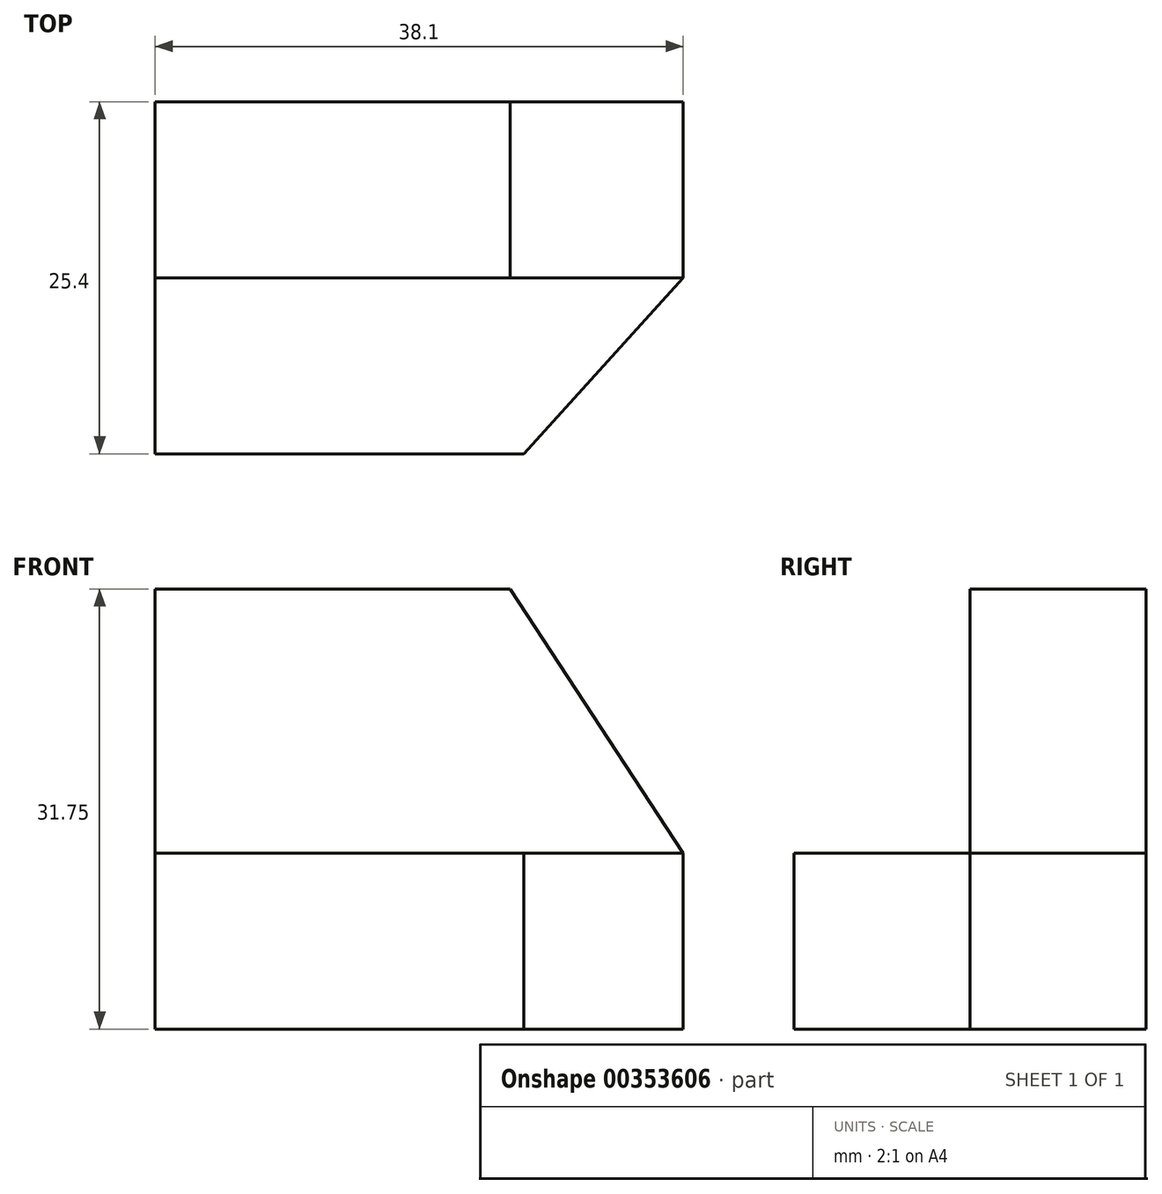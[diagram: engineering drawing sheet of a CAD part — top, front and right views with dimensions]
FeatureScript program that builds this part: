
annotation { "Feature Type Name" : "Feature", "Feature Type Description" : "" }
export const myFeature = defineFeature(function(context is Context, id is Id, definition is map)
    precondition{}
    {
        {
            var Q0;
            Q0=qCreatedBy(makeId("Right.planeOp"),FACE);
            var sketch = newSketch(context, id + "F0", { "sketchPlane" : qUnion([Q0])});
            skLineSegment(sketch, "E0", {"start": v(0, 0) * mm, "end": v(0, 31.75) * mm});
            skLineSegment(sketch, "E1", {"start": v(0, 31.75) * mm, "end": v(-12.7, 31.75) * mm});
            skLineSegment(sketch, "E2", {"start": v(-12.7, 31.75) * mm, "end": v(-12.7, 12.7) * mm});
            skLineSegment(sketch, "E3", {"start": v(-12.7, 12.7) * mm, "end": v(-25.4, 12.7) * mm});
            skLineSegment(sketch, "E4", {"start": v(-25.4, 12.7) * mm, "end": v(-25.4, 0) * mm});
            skLineSegment(sketch, "E5", {"start": v(-25.4, 0) * mm, "end": v(0, 0) * mm});
            skSolve(sketch);
        }
        {
            var Q0;
            Q0=makeQuery(id+"F0.imprint","IMPRINT",FACE,{"disambiguationData":[TD([[makeQuery(id+"F0.imprint","IMPRINT",EDGE,{"derivedFrom":sQuery(id+"F0.wireOp",EDGE,"E0")}),1.0]])]});
            extrude(context, id + "F1", {"entities" : qUnion([Q0]), "depth" : 38.1 * mm});
        }
        {
            var Q0;
            Q0=makeQuery(id+"F1.opExtrude","SWEPT_FACE",FACE,{"disambiguationData":[OSD([sQuery(id+"F0.wireOp",EDGE,"E3")])]});
            var sketch = newSketch(context, id + "F2", { "sketchPlane" : qUnion([Q0])});
            skLineSegment(sketch, "E6", {"start": v(38.1, -12.7) * mm, "end": v(26.61, -25.4) * mm});
            skLineSegment(sketch, "E7", {"start": v(26.61, -25.4) * mm, "end": v(38.1, -25.4) * mm});
            skLineSegment(sketch, "E8", {"start": v(38.1, -25.4) * mm, "end": v(38.1, -12.7) * mm});
            skSolve(sketch);
        }
        {
            var Q0;
            Q0=makeQuery(id+"F2.imprint","IMPRINT",FACE,{"disambiguationData":[TD([[makeQuery(id+"F2.imprint","IMPRINT",EDGE,{"derivedFrom":sQuery(id+"F2.wireOp",EDGE,"E6")}),1.0]])]});
            extrude(context, id + "F3", {"entities" : qUnion([Q0]), "operationType" : NewBodyOperationType.REMOVE, "oppositeDirection" : true, "depth" : 25.4 * mm});
        }
        {
            var Q0;
            Q0=makeQuery(id+"F1.opExtrude","SWEPT_FACE",FACE,{"disambiguationData":[OSD([sQuery(id+"F0.wireOp",EDGE,"E2")])]});
            var sketch = newSketch(context, id + "F4", { "sketchPlane" : qUnion([Q0])});
            skLineSegment(sketch, "E9", {"start": v(38.1, 12.7) * mm, "end": v(25.62, 31.75) * mm});
            skLineSegment(sketch, "E10", {"start": v(25.62, 31.75) * mm, "end": v(38.1, 31.75) * mm});
            skLineSegment(sketch, "E11", {"start": v(38.1, 31.75) * mm, "end": v(38.1, 12.7) * mm});
            skSolve(sketch);
        }
        {
            var Q0;
            Q0=makeQuery(id+"F4.imprint","IMPRINT",FACE,{"disambiguationData":[TD([[makeQuery(id+"F4.imprint","IMPRINT",EDGE,{"derivedFrom":sQuery(id+"F4.wireOp",EDGE,"E9")}),-1.0]])]});
            extrude(context, id + "F5", {"entities" : qUnion([Q0]), "operationType" : NewBodyOperationType.REMOVE, "oppositeDirection" : true, "depth" : 25.4 * mm});
        }
    });
